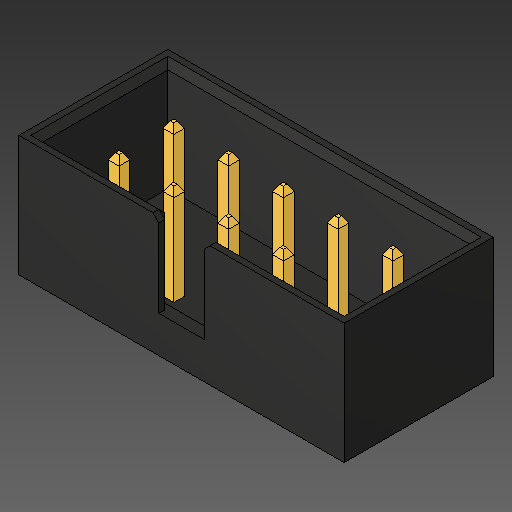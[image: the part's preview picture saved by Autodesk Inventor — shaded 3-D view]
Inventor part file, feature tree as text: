
AUTODESK INVENTOR PART (.ipt)
format: ipt  version: 2018.2 (Build 222227000, 227)  size: 160,256 bytes
history: native  units: mm
features: other x18, chamfer x2
ambient origin geometry x8: Origin, YZ Plane, XZ Plane, XY Plane, X Axis, Y Axis, Z Axis, Center Point
bodies: Body1 (feature_tree), Body2 (feature_tree), Body3 (feature_tree), Body4 (feature_tree), Body5 (feature_tree), Body6 (feature_tree), Body7 (feature_tree), Body8 (feature_tree), Body9 (feature_tree), Body10 (feature_tree)
feature tree (20):
  other  "ソリッド1"
  other  "ソリッド2"
  other  "ソリッド3"
  other  "ソリッド4"
  other  "ソリッド5"
  other  "ソリッド6"
  other  "ソリッド7"
  other  "ソリッド8"
  other  "ソリッド9"
  other  "ソリッド10"
  chamfer  "Chamfer1"  [1 undecoded]
  chamfer  "Chamfer2"  [1 undecoded]
  other  "LPattern3[1]"
  other  "LPattern3[2]"
  other  "LPattern3[3]"
  other  "LPattern3[4]"
  other  "LPattern3[5]"
  other  "LPattern3[6]"
  other  "LPattern3[7]"
  other  "LPattern3[8]"
note: 2 required parameter values undecoded (feature->parameter linkage not recoverable at this tier; creation-order binding heuristic only, values carry confidence <= 0.55)
